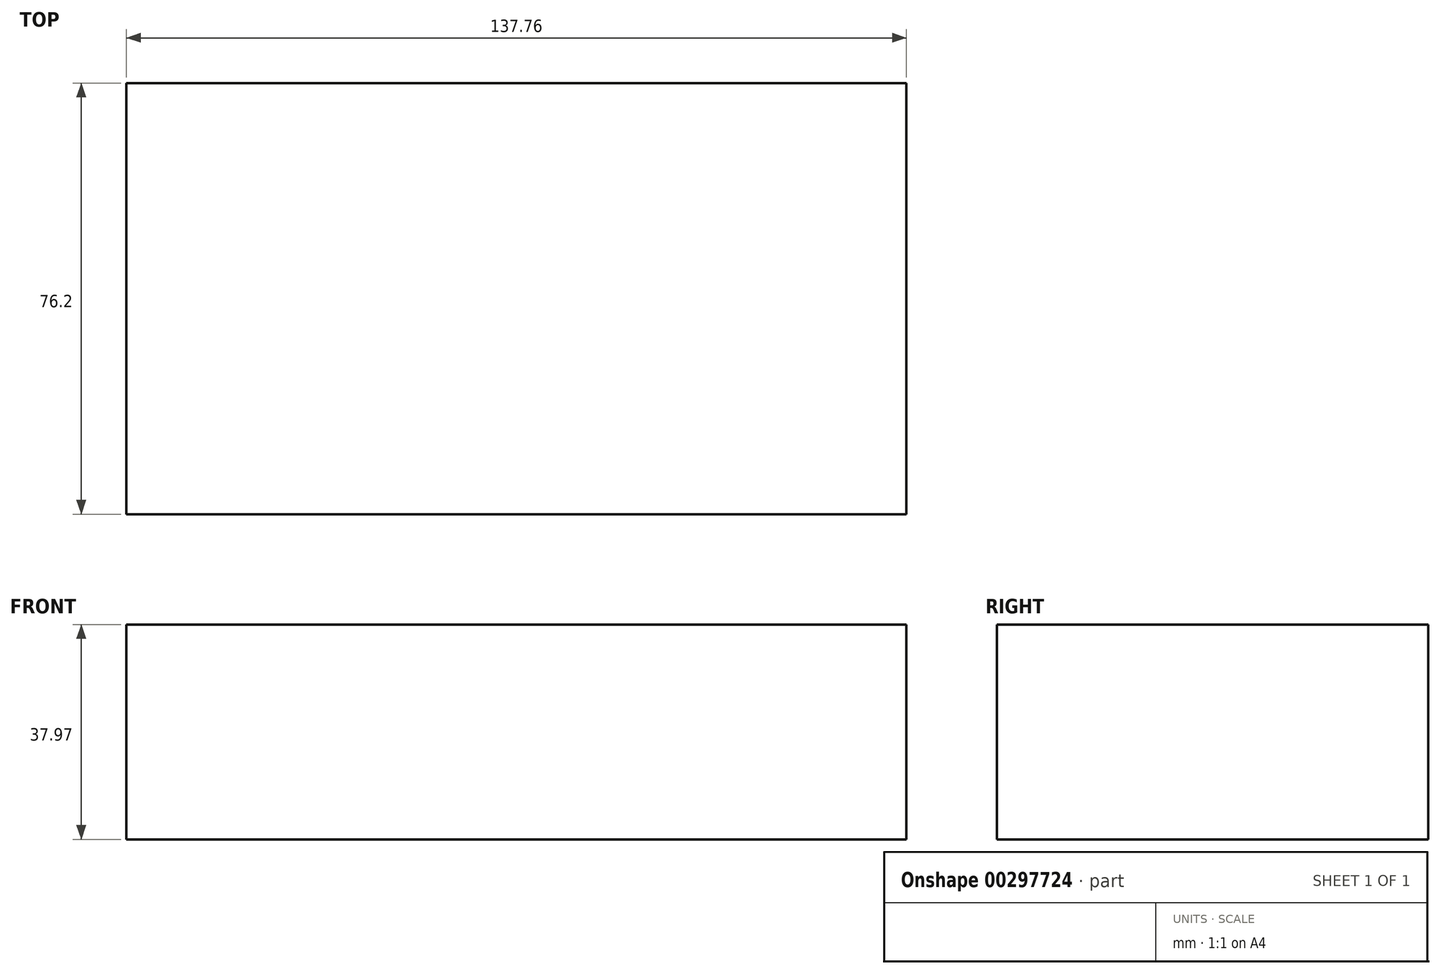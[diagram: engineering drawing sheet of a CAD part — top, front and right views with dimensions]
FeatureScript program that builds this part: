
annotation { "Feature Type Name" : "Feature", "Feature Type Description" : "" }
export const myFeature = defineFeature(function(context is Context, id is Id, definition is map)
    precondition{}
    {
        {
            var Q0;
            Q0=qCreatedBy(makeId("Front.planeOp"),FACE);
            var sketch = newSketch(context, id + "F0", { "sketchPlane" : qUnion([Q0])});
            skCircle(sketch, "E0", {"center": v(0, 0) * mm, "radius": 27.7 * mm});
            skLineSegment(sketch, "E1.bottom", {"start": v(-69.14, -27.9) * mm, "end": v(68.62, -27.9) * mm});
            skLineSegment(sketch, "E1.top", {"start": v(-69.14, -40.46) * mm, "end": v(68.62, -40.46) * mm});
            skLineSegment(sketch, "E1.left", {"start": v(-69.14, -27.9) * mm, "end": v(-69.14, -40.46) * mm});
            skLineSegment(sketch, "E1.right", {"start": v(68.62, -27.9) * mm, "end": v(68.62, -40.46) * mm});
            skCircle(sketch, "E2", {"center": v(0, 0) * mm, "radius": 8.35 * mm});
            skLineSegment(sketch, "E3", {"start": v(-69.14, -27.9) * mm, "end": v(-18.86, 20.3) * mm});
            skLineSegment(sketch, "E4", {"start": v(27.53, 3.13) * mm, "end": v(48.98, -27.9) * mm});
            skArc(sketch, "E5", {"start": v(-18.86, 20.3) * mm, "mid": v(-54.28, 6.93) * mm, "end": v(-69.14, -27.9) * mm});
            skSolve(sketch);
        }
        {
            var Q0;
            Q0=makeQuery(id+"F0.imprint","IMPRINT",FACE,{"disambiguationData":[TD([[makeQuery(id+"F0.imprint","IMPRINT",EDGE,{"derivedFrom":sQuery(id+"F0.wireOp",EDGE,"E1.top")}),1.0]])]});
            extrude(context, id + "F1", {"entities" : qUnion([Q0]), "depth" : 76.2 * mm});
        }
        {
            var Q0;
            Q0=makeQuery(id+"F1.opExtrude","SWEPT_FACE",FACE,{"disambiguationData":[OSD([sQuery(id+"F0.wireOp",EDGE,"E1.bottom")])]});
            extrude(context, id + "F2", {"entities" : qUnion([Q0]), "operationType" : NewBodyOperationType.ADD, "depth" : 25.4 * mm});
        }
    });
